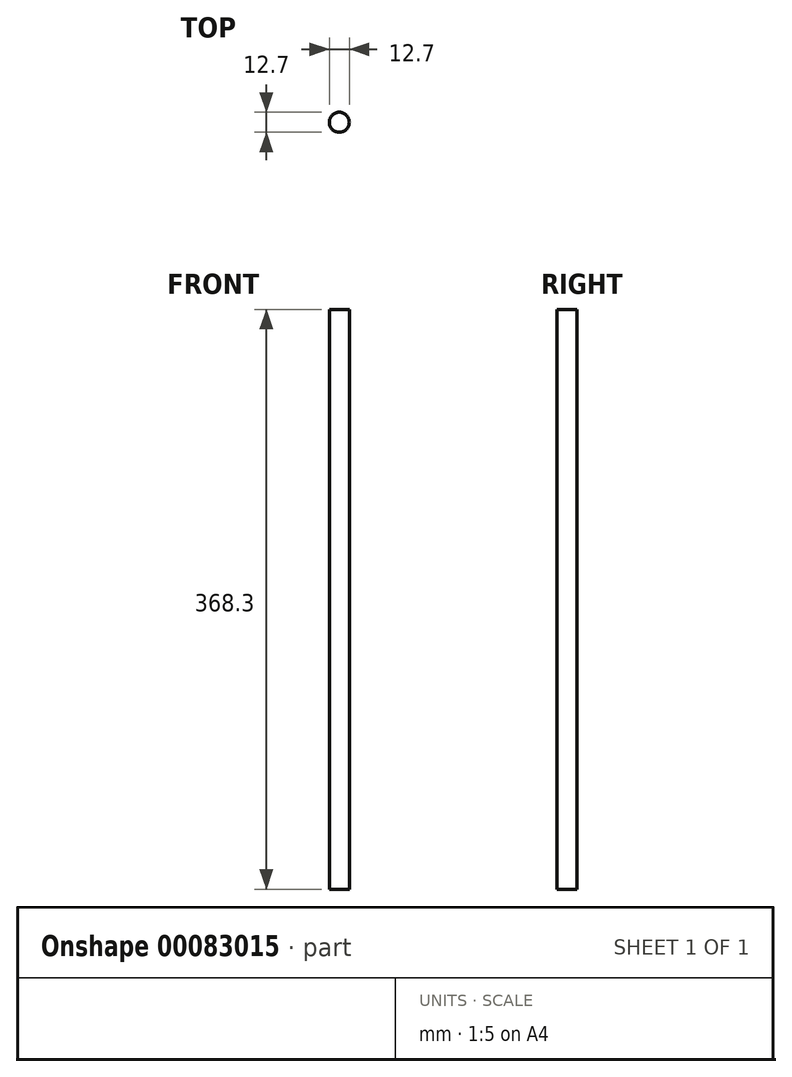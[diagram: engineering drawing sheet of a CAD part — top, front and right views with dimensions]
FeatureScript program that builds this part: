
annotation { "Feature Type Name" : "Feature", "Feature Type Description" : "" }
export const myFeature = defineFeature(function(context is Context, id is Id, definition is map)
    precondition{}
    {
        {
            var Q0;
            Q0=qCreatedBy(makeId("Top.planeOp"),FACE);
            var sketch = newSketch(context, id + "F0", { "sketchPlane" : qUnion([Q0])});
            skCircle(sketch, "E0", {"center": v(0, 0) * mm, "radius": 6.35 * mm});
            skSolve(sketch);
        }
        {
            var Q0;
            Q0=makeQuery(id+"F0.imprint","IMPRINT",FACE,{"disambiguationData":[TD([[makeQuery(id+"F0.imprint","IMPRINT",EDGE,{"derivedFrom":sQuery(id+"F0.wireOp",EDGE,"E0")}),1.0]])]});
            extrude(context, id + "F1", {"entities" : qUnion([Q0]), "depth" : 368.3 * mm});
        }
    });
